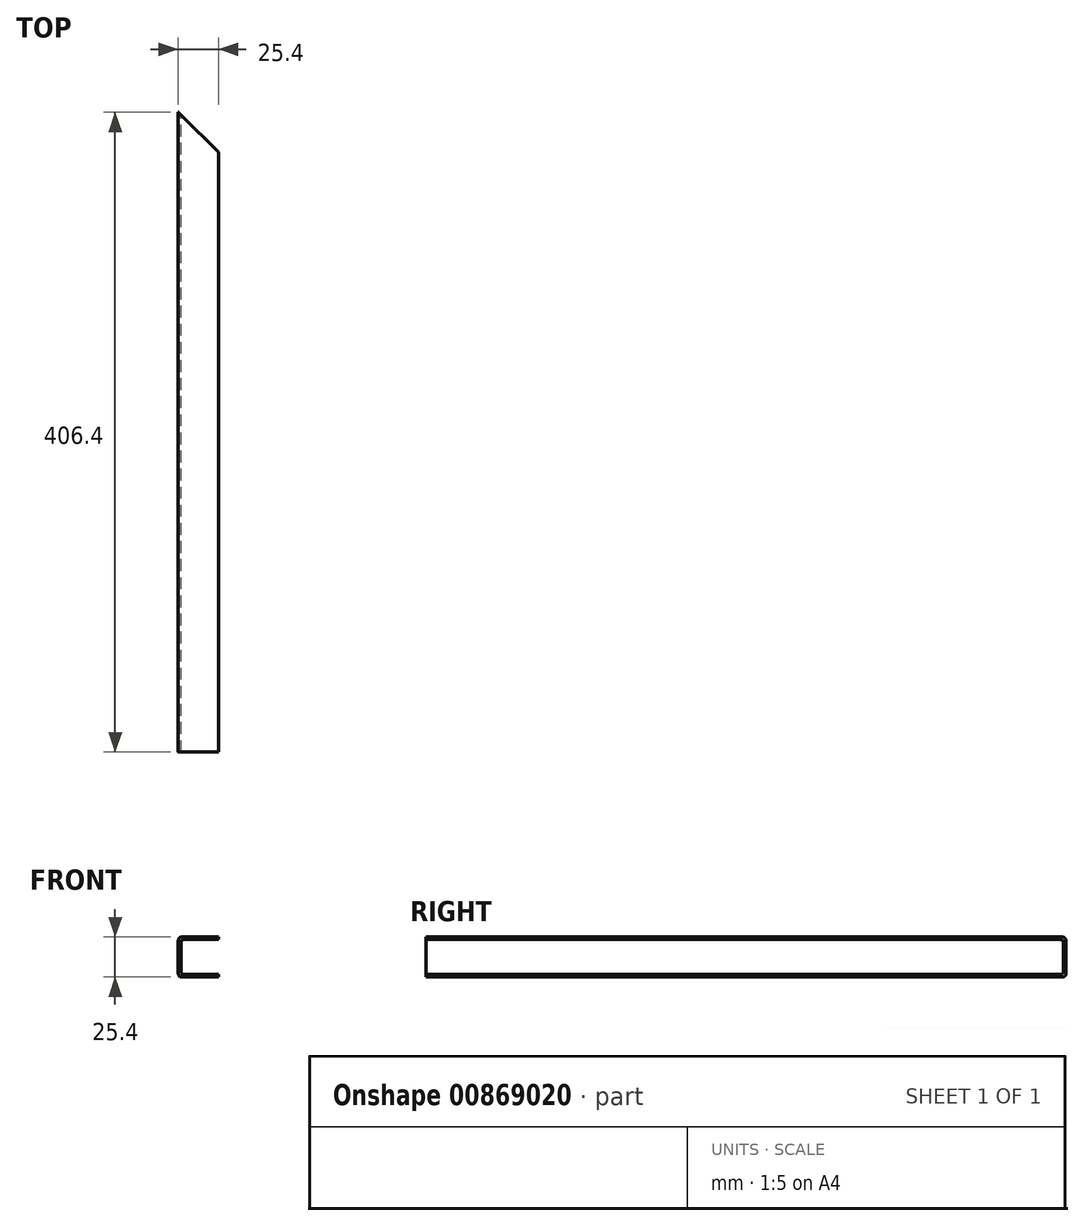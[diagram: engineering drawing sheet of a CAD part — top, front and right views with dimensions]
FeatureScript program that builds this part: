
annotation { "Feature Type Name" : "Feature", "Feature Type Description" : "" }
export const myFeature = defineFeature(function(context is Context, id is Id, definition is map)
    precondition{}
    {
        {
            var Q0;
            Q0=qCreatedBy(makeId("Front.planeOp"),FACE);
            var sketch = newSketch(context, id + "F0", { "sketchPlane" : qUnion([Q0])});
            skLineSegment(sketch, "E0.bottom", {"start": v(-23.37, 12.7) * mm, "end": v(0, 12.7) * mm});
            skLineSegment(sketch, "E0.top", {"start": v(-23.37, -12.7) * mm, "end": v(0, -12.7) * mm});
            skLineSegment(sketch, "E0.left", {"start": v(-25.4, 10.67) * mm, "end": v(-25.4, -10.67) * mm});
            skPoint(sketch, "E0.middle", {"position": v(0, 0) * mm});
            skPoint(sketch, "E1.visualSharp", {"position": v(25.4, 12.7) * mm});
            skPoint(sketch, "E2.visualSharp", {"position": v(25.4, -12.7) * mm});
            skPoint(sketch, "E3.visualSharp", {"position": v(-25.4, -12.7) * mm});
            skArc(sketch, "E3.filletArc", {"start": v(-25.4, -10.67) * mm, "mid": v(-24.8, -12.1) * mm, "end": v(-23.37, -12.7) * mm});
            skPoint(sketch, "E4.visualSharp", {"position": v(-25.4, 12.7) * mm});
            skArc(sketch, "E4.filletArc", {"start": v(-23.37, 12.7) * mm, "mid": v(-24.8, 12.1) * mm, "end": v(-25.4, 10.67) * mm});
            skLineSegment(sketch, "E5.1", {"start": v(-21.78, 11.11) * mm, "end": v(0, 11.11) * mm});
            skLineSegment(sketch, "E5.2", {"start": v(-23.81, 9.08) * mm, "end": v(-23.81, -9.08) * mm});
            skLineSegment(sketch, "E5.3", {"start": v(-21.78, -11.11) * mm, "end": v(0, -11.11) * mm});
            skPoint(sketch, "E6.visualSharp", {"position": v(-23.81, 11.11) * mm});
            skArc(sketch, "E6.filletArc", {"start": v(-21.78, 11.11) * mm, "mid": v(-23.22, 10.52) * mm, "end": v(-23.81, 9.08) * mm});
            skPoint(sketch, "E7.visualSharp", {"position": v(-23.81, -11.11) * mm});
            skArc(sketch, "E7.filletArc", {"start": v(-23.81, -9.08) * mm, "mid": v(-23.22, -10.52) * mm, "end": v(-21.78, -11.11) * mm});
            skPoint(sketch, "E8.visualSharp", {"position": v(23.81, 11.11) * mm});
            skPoint(sketch, "E9.visualSharp", {"position": v(23.81, -11.11) * mm});
            skLineSegment(sketch, "E10", {"start": v(0, 12.7) * mm, "end": v(0, 11.11) * mm});
            skLineSegment(sketch, "E11.trimOffspring", {"start": v(0, -11.11) * mm, "end": v(0, -12.7) * mm});
            skPoint(sketch, "E1.filletArc.end.orphan", {"position": v(23.37, 12.7) * mm});
            skPoint(sketch, "E2.filletArc.start.orphan", {"position": v(23.37, -12.7) * mm});
            skSolve(sketch);
        }
        {
            var Q0;
            Q0 = qSketchRegion(id + "F0", true);
            extrude(context, id + "F1", {"entities" : qUnion([Q0]), "depth" : 406.4 * mm, "offsetDistance" : 25.4 * mm});
        }
        {
            var Q0;
            Q0=qCreatedBy(makeId("Top.planeOp"),FACE);
            var sketch = newSketch(context, id + "F2", { "sketchPlane" : qUnion([Q0])});
            skLineSegment(sketch, "E12", {"start": v(0, 0) * mm, "end": v(0, -25.4) * mm});
            skLineSegment(sketch, "E13", {"start": v(0, -25.4) * mm, "end": v(-25.4, 0) * mm});
            skLineSegment(sketch, "E14.0", {"start": v(-25.4, -406.4) * mm, "end": v(-25.4, 0) * mm, "construction": true});
            skLineSegment(sketch, "E15", {"start": v(-25.4, 0) * mm, "end": v(0, 0) * mm});
            skSolve(sketch);
        }
        {
            var Q0;
            Q0 = qSketchRegion(id + "F2", true);
            extrude(context, id + "F3", {"entities" : qUnion([Q0]), "operationType" : NewBodyOperationType.REMOVE, "oppositeDirection" : true, "depth" : 76.2 * mm, "offsetDistance" : 25.4 * mm, "symmetric" : true});
        }
    });
